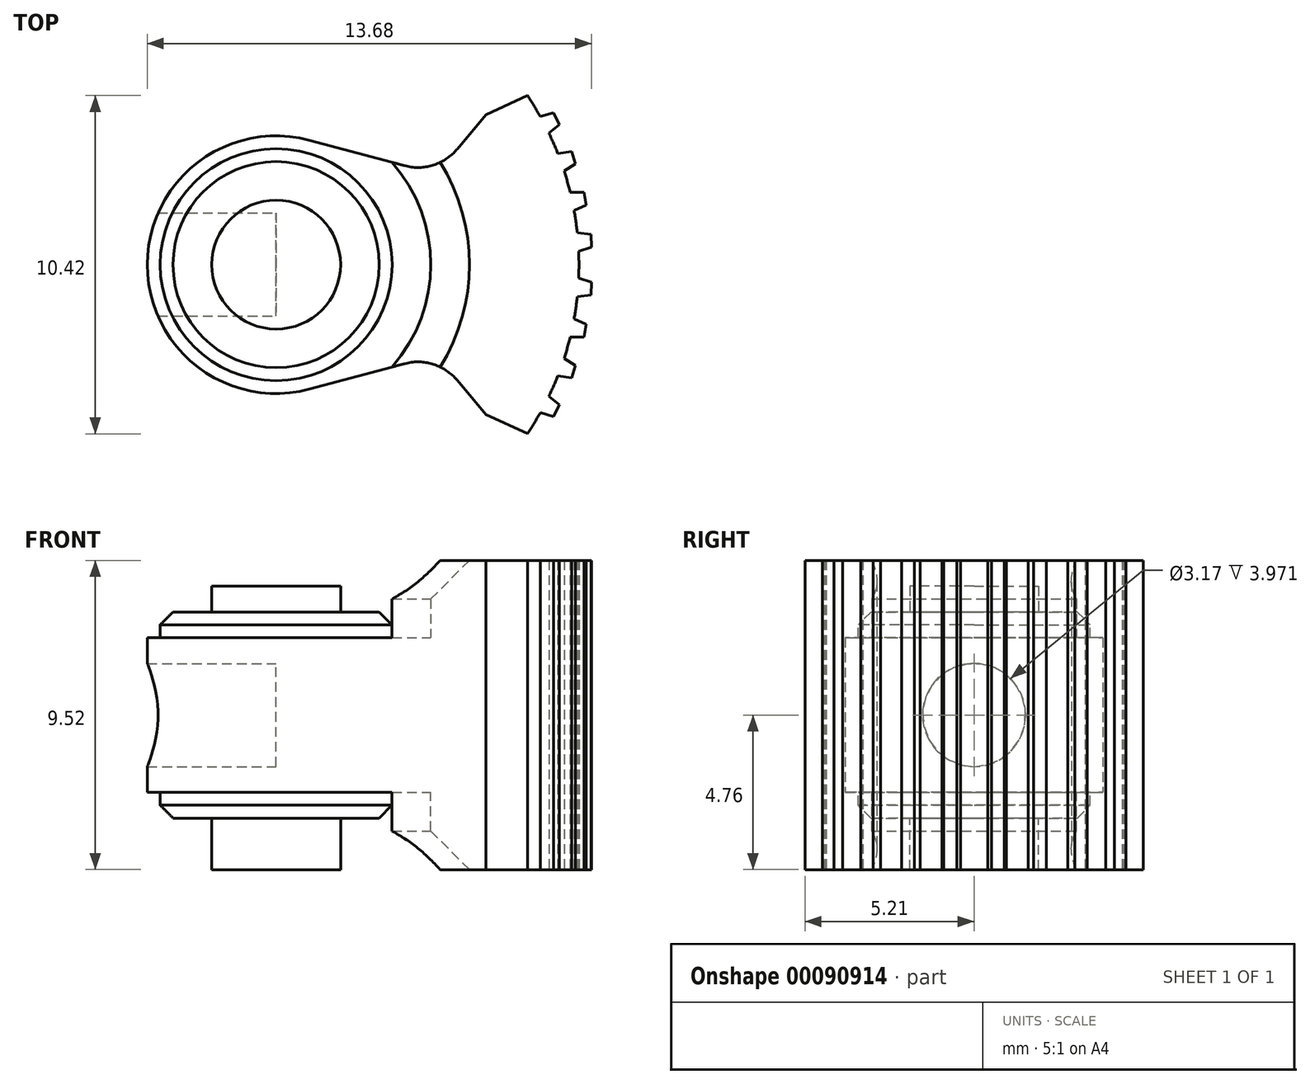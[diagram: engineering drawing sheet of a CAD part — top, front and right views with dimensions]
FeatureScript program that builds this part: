
annotation { "Feature Type Name" : "Feature", "Feature Type Description" : "" }
export const myFeature = defineFeature(function(context is Context, id is Id, definition is map)
    precondition{}
    {
        {
            var Q0;
            Q0=qCreatedBy(makeId("Top.planeOp"),FACE);
            var sketch = newSketch(context, id + "F0", { "sketchPlane" : qUnion([Q0])});
            skCircle(sketch, "E0", {"center": v(0, 0) * mm, "radius": 3.57 * mm});
            skCircle(sketch, "E1", {"center": v(0, 0) * mm, "radius": 1.98 * mm});
            skArc(sketch, "E2", {"start": v(3.57, -3.15) * mm, "mid": v(4.76, 0) * mm, "end": v(3.57, 3.15) * mm});
            skArc(sketch, "E3", {"start": v(6.46, -4.61) * mm, "mid": v(7.94, 0) * mm, "end": v(6.46, 4.61) * mm});
            skArc(sketch, "E4", {"start": v(7.74, -5.2) * mm, "mid": v(9.33, 0) * mm, "end": v(7.74, 5.2) * mm});
            skCircle(sketch, "E5.converted", {"center": v(0, 0) * mm, "radius": 3.97 * mm});
            skLineSegment(sketch, "E6", {"start": v(0, 0) * mm, "end": v(19.98, 0) * mm, "construction": true});
            skLineSegment(sketch, "E7", {"start": v(1.03, 3.83) * mm, "end": v(3.95, 3.05) * mm});
            skLineSegment(sketch, "E8", {"start": v(1.03, -3.83) * mm, "end": v(3.95, -3.05) * mm});
            skLineSegment(sketch, "E9", {"start": v(5.58, 3.56) * mm, "end": v(6.46, 4.61) * mm});
            skLineSegment(sketch, "E10", {"start": v(5.58, -3.56) * mm, "end": v(6.46, -4.61) * mm});
            skArc(sketch, "E11.filletArc", {"start": v(3.95, 3.05) * mm, "mid": v(4.84, 3.07) * mm, "end": v(5.58, 3.56) * mm});
            skArc(sketch, "E12.filletArc", {"start": v(5.58, -3.56) * mm, "mid": v(4.84, -3.07) * mm, "end": v(3.95, -3.05) * mm});
            skLineSegment(sketch, "E13", {"start": v(6.46, 4.61) * mm, "end": v(7.74, 5.2) * mm});
            skLineSegment(sketch, "E14", {"start": v(6.46, -4.61) * mm, "end": v(7.74, -5.2) * mm});
            skLineSegment(sketch, "E15.1.0", {"start": v(9.27, -0.99) * mm, "end": v(9.7, -0.93) * mm});
            skLineSegment(sketch, "E15.1.1", {"start": v(9.7, -0.93) * mm, "end": v(9.71, -0.53) * mm});
            skLineSegment(sketch, "E15.1.2", {"start": v(9.71, -0.53) * mm, "end": v(9.31, -0.42) * mm});
            skLineSegment(sketch, "E15.2.0", {"start": v(9.05, -2.23) * mm, "end": v(9.49, -2.23) * mm});
            skLineSegment(sketch, "E15.2.1", {"start": v(9.49, -2.23) * mm, "end": v(9.55, -1.84) * mm});
            skLineSegment(sketch, "E15.2.2", {"start": v(9.55, -1.84) * mm, "end": v(9.17, -1.67) * mm});
            skLineSegment(sketch, "E15.3.0", {"start": v(8.67, -3.42) * mm, "end": v(9.1, -3.49) * mm});
            skLineSegment(sketch, "E15.3.1", {"start": v(9.1, -3.49) * mm, "end": v(9.22, -3.1) * mm});
            skLineSegment(sketch, "E15.3.2", {"start": v(9.22, -3.1) * mm, "end": v(8.87, -2.88) * mm});
            skLineSegment(sketch, "E15.4.0", {"start": v(8.13, -4.56) * mm, "end": v(8.55, -4.68) * mm});
            skLineSegment(sketch, "E15.4.1", {"start": v(8.55, -4.68) * mm, "end": v(8.72, -4.31) * mm});
            skLineSegment(sketch, "E15.4.2", {"start": v(8.72, -4.31) * mm, "end": v(8.4, -4.05) * mm});
            skLineSegment(sketch, "E15.anchor1", {"start": v(0, 0) * mm, "end": v(9.29, 0.84) * mm, "construction": true});
            skLineSegment(sketch, "E15.anchor2", {"start": v(0, 0) * mm, "end": v(8.4, -4.05) * mm, "construction": true});
            skLineSegment(sketch, "E16.MirrorCS", {"start": v(9.7, 0.93) * mm, "end": v(9.71, 0.53) * mm});
            skLineSegment(sketch, "E17.MirrorCS", {"start": v(9.71, 0.53) * mm, "end": v(9.31, 0.42) * mm});
            skLineSegment(sketch, "E18.MirrorCS", {"start": v(9.27, 0.99) * mm, "end": v(9.7, 0.93) * mm});
            skLineSegment(sketch, "E19.MirrorCS", {"start": v(9.05, 2.23) * mm, "end": v(9.49, 2.23) * mm});
            skLineSegment(sketch, "E20.MirrorCS", {"start": v(9.55, 1.84) * mm, "end": v(9.17, 1.67) * mm});
            skLineSegment(sketch, "E21.MirrorCS", {"start": v(9.49, 2.23) * mm, "end": v(9.55, 1.84) * mm});
            skLineSegment(sketch, "E22.MirrorCS", {"start": v(9.1, 3.49) * mm, "end": v(9.22, 3.1) * mm});
            skLineSegment(sketch, "E23.MirrorCS", {"start": v(8.67, 3.42) * mm, "end": v(9.1, 3.49) * mm});
            skLineSegment(sketch, "E24.MirrorCS", {"start": v(9.22, 3.1) * mm, "end": v(8.87, 2.88) * mm});
            skLineSegment(sketch, "E25.MirrorCS", {"start": v(8.13, 4.56) * mm, "end": v(8.55, 4.68) * mm});
            skLineSegment(sketch, "E26.MirrorCS", {"start": v(8.55, 4.68) * mm, "end": v(8.72, 4.31) * mm});
            skLineSegment(sketch, "E27.MirrorCS", {"start": v(8.72, 4.31) * mm, "end": v(8.4, 4.05) * mm});
            skSolve(sketch);
        }
        {
            var Q0;
            Q0=makeQuery(id+"F0.imprint","IMPRINT",FACE,{"disambiguationData":[TD([[makeQuery(id+"F0.imprint","IMPRINT",EDGE,{"derivedFrom":sQuery(id+"F0.wireOp",EDGE,"E1")}),1.0]])]});
            var Q1;
            Q1=makeQuery(id+"F0.imprint","IMPRINT",FACE,{"disambiguationData":[TD([[makeQuery(id+"F0.imprint","IMPRINT",EDGE,{"derivedFrom":sQuery(id+"F0.wireOp",EDGE,"E0")}),1.0]])]});
            var Q2;
            Q2=makeQuery(id+"F0.imprint","IMPRINT",FACE,{"disambiguationData":[TD([[makeQuery(id+"F0.imprint","IMPRINT",EDGE,{"derivedFrom":sQuery(id+"F0.wireOp",EDGE,"E0")}),-1.0]])]});
            var Q3;
            {var subQ0=sQuery(id+"F0.wireOp",EDGE,"E2");Q3=makeQuery(id+"F0.imprint","IMPRINT",FACE,{"disambiguationData":[TD([[makeQuery(id+"F0.imprint","IMPRINT",EDGE,{"derivedFrom":subQ0}),1.0]])]});}
            var Q4;
            {var subQ1=sQuery(id+"F0.wireOp",EDGE,"E2");Q4=makeQuery(id+"F0.imprint","IMPRINT",FACE,{"disambiguationData":[TD([[makeQuery(id+"F0.imprint","IMPRINT",EDGE,{"derivedFrom":subQ1}),-1.0]])]});}
            var Q5;
            Q5=makeQuery(id+"F0.imprint","IMPRINT",FACE,{"disambiguationData":[TD([[makeQuery(id+"F0.imprint","IMPRINT",EDGE,{"derivedFrom":sQuery(id+"F0.wireOp",EDGE,"E3")}),-1.0]])]});
            var Q6;
            {var subQ0=sQuery(id+"F0.wireOp",EDGE,"E15.4.0");Q6=makeQuery(id+"F0.imprint","IMPRINT",FACE,{"disambiguationData":[TD([[makeQuery(id+"F0.imprint","IMPRINT",EDGE,{"derivedFrom":subQ0}),1.0]])]});}
            var Q7;
            {var subQ0=sQuery(id+"F0.wireOp",EDGE,"E15.3.0");Q7=makeQuery(id+"F0.imprint","IMPRINT",FACE,{"disambiguationData":[TD([[makeQuery(id+"F0.imprint","IMPRINT",EDGE,{"derivedFrom":subQ0}),1.0]])]});}
            var Q8;
            {var subQ0=sQuery(id+"F0.wireOp",EDGE,"E15.2.0");Q8=makeQuery(id+"F0.imprint","IMPRINT",FACE,{"disambiguationData":[TD([[makeQuery(id+"F0.imprint","IMPRINT",EDGE,{"derivedFrom":subQ0}),1.0]])]});}
            var Q9;
            {var subQ0=sQuery(id+"F0.wireOp",EDGE,"E15.1.0");Q9=makeQuery(id+"F0.imprint","IMPRINT",FACE,{"disambiguationData":[TD([[makeQuery(id+"F0.imprint","IMPRINT",EDGE,{"derivedFrom":subQ0}),1.0]])]});}
            var Q10;
            Q10=makeQuery(id+"F0.imprint","IMPRINT",FACE,{"disambiguationData":[TD([[makeQuery(id+"F0.imprint","IMPRINT",EDGE,{"derivedFrom":sQuery(id+"F0.wireOp",EDGE,"E16.MirrorCS")}),-1.0]])]});
            var Q11;
            {var subQ0=sQuery(id+"F0.wireOp",EDGE,"E19.MirrorCS");Q11=makeQuery(id+"F0.imprint","IMPRINT",FACE,{"disambiguationData":[TD([[makeQuery(id+"F0.imprint","IMPRINT",EDGE,{"derivedFrom":subQ0}),-1.0]])]});}
            var Q12;
            Q12=makeQuery(id+"F0.imprint","IMPRINT",FACE,{"disambiguationData":[TD([[makeQuery(id+"F0.imprint","IMPRINT",EDGE,{"derivedFrom":sQuery(id+"F0.wireOp",EDGE,"E22.MirrorCS")}),-1.0]])]});
            var Q13;
            {var subQ0=sQuery(id+"F0.wireOp",EDGE,"E25.MirrorCS");Q13=makeQuery(id+"F0.imprint","IMPRINT",FACE,{"disambiguationData":[TD([[makeQuery(id+"F0.imprint","IMPRINT",EDGE,{"derivedFrom":subQ0}),-1.0]])]});}
            extrude(context, id + "F1", {"entities" : qUnion([Q0, Q1, Q2, Q3, Q4, Q5, Q6, Q7, Q8, Q9, Q10, Q11, Q12, Q13]), "endBound" : BoundingType.SYMMETRIC, "depth" : 9.52 * mm});
        }
        {
            var Q0;
            Q0=makeQuery(id+"F1.opExtrude","CAP_FACE",FACE,{"disambiguationData":[OSD([sQuery(id+"F0.wireOp",EDGE,"E4"),sQuery(id+"F0.wireOp",EDGE,"E5.converted"),sQuery(id+"F0.wireOp",EDGE,"E7"),sQuery(id+"F0.wireOp",EDGE,"E8"),sQuery(id+"F0.wireOp",EDGE,"E9"),sQuery(id+"F0.wireOp",EDGE,"E10"),sQuery(id+"F0.wireOp",EDGE,"E11.filletArc"),sQuery(id+"F0.wireOp",EDGE,"E12.filletArc"),sQuery(id+"F0.wireOp",EDGE,"E13"),sQuery(id+"F0.wireOp",EDGE,"E14"),sQuery(id+"F0.wireOp",EDGE,"E15.1.0"),sQuery(id+"F0.wireOp",EDGE,"E15.1.1"),sQuery(id+"F0.wireOp",EDGE,"E15.1.2"),sQuery(id+"F0.wireOp",EDGE,"E15.2.0"),sQuery(id+"F0.wireOp",EDGE,"E15.2.1"),sQuery(id+"F0.wireOp",EDGE,"E15.2.2"),sQuery(id+"F0.wireOp",EDGE,"E15.3.0"),sQuery(id+"F0.wireOp",EDGE,"E15.3.1"),sQuery(id+"F0.wireOp",EDGE,"E15.3.2"),sQuery(id+"F0.wireOp",EDGE,"E15.4.0"),sQuery(id+"F0.wireOp",EDGE,"E15.4.1"),sQuery(id+"F0.wireOp",EDGE,"E15.4.2"),sQuery(id+"F0.wireOp",EDGE,"E16.MirrorCS"),sQuery(id+"F0.wireOp",EDGE,"E17.MirrorCS"),sQuery(id+"F0.wireOp",EDGE,"E18.MirrorCS"),sQuery(id+"F0.wireOp",EDGE,"E19.MirrorCS"),sQuery(id+"F0.wireOp",EDGE,"E20.MirrorCS"),sQuery(id+"F0.wireOp",EDGE,"E21.MirrorCS"),sQuery(id+"F0.wireOp",EDGE,"E22.MirrorCS"),sQuery(id+"F0.wireOp",EDGE,"E23.MirrorCS"),sQuery(id+"F0.wireOp",EDGE,"E24.MirrorCS"),sQuery(id+"F0.wireOp",EDGE,"E25.MirrorCS"),sQuery(id+"F0.wireOp",EDGE,"E26.MirrorCS"),sQuery(id+"F0.wireOp",EDGE,"E27.MirrorCS")])],"isStart":false});
            var Q1;
            Q1 = qBodyType(qCreatedBy(id + "F3" ,EDGE), BodyType.WIRE);
            cPlane(context, id + "F2", {"entities" : qUnion([Q0, Q1]), "cplaneType" : CPlaneType.OFFSET, "offset" : 2.38 * mm, "oppositeDirection" : true, "width" : 152.4 * mm, "height" : 152.4 * mm});
        }
        {
            var Q0;
            Q0=qCreatedBy(id+"F2.planeOp",FACE);
            var sketch = newSketch(context, id + "F3", { "sketchPlane" : qUnion([Q0])});
            skCircle(sketch, "E28", {"center": v(0, 0) * mm, "radius": 4.76 * mm});
            skSolve(sketch);
        }
        {
            var Q0;
            Q0=makeQuery(id+"F3.imprint","IMPRINT",FACE,{"disambiguationData":[TD([[makeQuery(id+"F3.imprint","IMPRINT",EDGE,{"derivedFrom":sQuery(id+"F3.wireOp",EDGE,"E28")}),1.0]])]});
            extrude(context, id + "F4", {"entities" : qUnion([Q0]), "operationType" : NewBodyOperationType.REMOVE, "depth" : 6.35 * mm});
        }
        {
            var Q0;
            Q0=makeQuery(id+"F1.opExtrude","CAP_FACE",FACE,{"disambiguationData":[OSD([sQuery(id+"F0.wireOp",EDGE,"E4"),sQuery(id+"F0.wireOp",EDGE,"E5.converted"),sQuery(id+"F0.wireOp",EDGE,"E7"),sQuery(id+"F0.wireOp",EDGE,"E8"),sQuery(id+"F0.wireOp",EDGE,"E9"),sQuery(id+"F0.wireOp",EDGE,"E10"),sQuery(id+"F0.wireOp",EDGE,"E11.filletArc"),sQuery(id+"F0.wireOp",EDGE,"E12.filletArc"),sQuery(id+"F0.wireOp",EDGE,"E13"),sQuery(id+"F0.wireOp",EDGE,"E14"),sQuery(id+"F0.wireOp",EDGE,"E15.1.0"),sQuery(id+"F0.wireOp",EDGE,"E15.1.1"),sQuery(id+"F0.wireOp",EDGE,"E15.1.2"),sQuery(id+"F0.wireOp",EDGE,"E15.2.0"),sQuery(id+"F0.wireOp",EDGE,"E15.2.1"),sQuery(id+"F0.wireOp",EDGE,"E15.2.2"),sQuery(id+"F0.wireOp",EDGE,"E15.3.0"),sQuery(id+"F0.wireOp",EDGE,"E15.3.1"),sQuery(id+"F0.wireOp",EDGE,"E15.3.2"),sQuery(id+"F0.wireOp",EDGE,"E15.4.0"),sQuery(id+"F0.wireOp",EDGE,"E15.4.1"),sQuery(id+"F0.wireOp",EDGE,"E15.4.2"),sQuery(id+"F0.wireOp",EDGE,"E16.MirrorCS"),sQuery(id+"F0.wireOp",EDGE,"E17.MirrorCS"),sQuery(id+"F0.wireOp",EDGE,"E18.MirrorCS"),sQuery(id+"F0.wireOp",EDGE,"E19.MirrorCS"),sQuery(id+"F0.wireOp",EDGE,"E20.MirrorCS"),sQuery(id+"F0.wireOp",EDGE,"E21.MirrorCS"),sQuery(id+"F0.wireOp",EDGE,"E22.MirrorCS"),sQuery(id+"F0.wireOp",EDGE,"E23.MirrorCS"),sQuery(id+"F0.wireOp",EDGE,"E24.MirrorCS"),sQuery(id+"F0.wireOp",EDGE,"E25.MirrorCS"),sQuery(id+"F0.wireOp",EDGE,"E26.MirrorCS"),sQuery(id+"F0.wireOp",EDGE,"E27.MirrorCS")])],"isStart":true});
            cPlane(context, id + "F5", {"entities" : qUnion([Q0]), "cplaneType" : CPlaneType.OFFSET, "offset" : 4.76 * mm, "oppositeDirection" : true, "width" : 152.4 * mm, "height" : 152.4 * mm});
        }
        {
            var Q0;
            Q0=makeQuery(id+"F1.opExtrude","CAP_FACE",FACE,{"disambiguationData":[OSD([sQuery(id+"F0.wireOp",EDGE,"E4"),sQuery(id+"F0.wireOp",EDGE,"E5.converted"),sQuery(id+"F0.wireOp",EDGE,"E7"),sQuery(id+"F0.wireOp",EDGE,"E8"),sQuery(id+"F0.wireOp",EDGE,"E9"),sQuery(id+"F0.wireOp",EDGE,"E10"),sQuery(id+"F0.wireOp",EDGE,"E11.filletArc"),sQuery(id+"F0.wireOp",EDGE,"E12.filletArc"),sQuery(id+"F0.wireOp",EDGE,"E13"),sQuery(id+"F0.wireOp",EDGE,"E14"),sQuery(id+"F0.wireOp",EDGE,"E15.1.0"),sQuery(id+"F0.wireOp",EDGE,"E15.1.1"),sQuery(id+"F0.wireOp",EDGE,"E15.1.2"),sQuery(id+"F0.wireOp",EDGE,"E15.2.0"),sQuery(id+"F0.wireOp",EDGE,"E15.2.1"),sQuery(id+"F0.wireOp",EDGE,"E15.2.2"),sQuery(id+"F0.wireOp",EDGE,"E15.3.0"),sQuery(id+"F0.wireOp",EDGE,"E15.3.1"),sQuery(id+"F0.wireOp",EDGE,"E15.3.2"),sQuery(id+"F0.wireOp",EDGE,"E15.4.0"),sQuery(id+"F0.wireOp",EDGE,"E15.4.1"),sQuery(id+"F0.wireOp",EDGE,"E15.4.2"),sQuery(id+"F0.wireOp",EDGE,"E16.MirrorCS"),sQuery(id+"F0.wireOp",EDGE,"E17.MirrorCS"),sQuery(id+"F0.wireOp",EDGE,"E18.MirrorCS"),sQuery(id+"F0.wireOp",EDGE,"E19.MirrorCS"),sQuery(id+"F0.wireOp",EDGE,"E20.MirrorCS"),sQuery(id+"F0.wireOp",EDGE,"E21.MirrorCS"),sQuery(id+"F0.wireOp",EDGE,"E22.MirrorCS"),sQuery(id+"F0.wireOp",EDGE,"E23.MirrorCS"),sQuery(id+"F0.wireOp",EDGE,"E24.MirrorCS"),sQuery(id+"F0.wireOp",EDGE,"E25.MirrorCS"),sQuery(id+"F0.wireOp",EDGE,"E26.MirrorCS"),sQuery(id+"F0.wireOp",EDGE,"E27.MirrorCS")])],"isStart":true});
            cPlane(context, id + "F6", {"entities" : qUnion([Q0]), "cplaneType" : CPlaneType.OFFSET, "offset" : 2.38 * mm, "oppositeDirection" : true, "width" : 152.4 * mm, "height" : 152.4 * mm});
        }
        {
            var Q0;
            Q0=qCreatedBy(id+"F6.planeOp",FACE);
            var sketch = newSketch(context, id + "F7", { "sketchPlane" : qUnion([Q0])});
            skCircle(sketch, "E29", {"center": v(0, 0) * mm, "radius": 4.76 * mm});
            skSolve(sketch);
        }
        {
            var Q0;
            Q0=makeQuery(id+"F7.imprint","IMPRINT",FACE,{"disambiguationData":[TD([[makeQuery(id+"F7.imprint","IMPRINT",EDGE,{"derivedFrom":sQuery(id+"F7.wireOp",EDGE,"E29")}),1.0]])]});
            extrude(context, id + "F8", {"entities" : qUnion([Q0]), "operationType" : NewBodyOperationType.REMOVE, "depth" : 4.3 * mm});
        }
        {
            var Q0;
            Q0=qCreatedBy(id+"F5.planeOp",FACE);
            var sketch = newSketch(context, id + "F9", { "sketchPlane" : qUnion([Q0])});
            skCircle(sketch, "E30", {"center": v(0, 0) * mm, "radius": 3.57 * mm});
            skSolve(sketch);
        }
        {
            var Q0;
            Q0 = qSketchRegion(id + "F9", true);
            extrude(context, id + "F10", {"entities" : qUnion([Q0]), "operationType" : NewBodyOperationType.ADD, "endBound" : BoundingType.SYMMETRIC, "depth" : 6.35 * mm});
        }
        {
            var Q0;
            Q0=qCreatedBy(id+"F2.planeOp",FACE);
            var sketch = newSketch(context, id + "F11", { "sketchPlane" : qUnion([Q0])});
            skCircle(sketch, "E31", {"center": v(0, 0) * mm, "radius": 1.98 * mm});
            skSolve(sketch);
        }
        {
            var Q0;
            Q0 = qSketchRegion(id + "F11", true);
            extrude(context, id + "F12", {"entities" : qUnion([Q0]), "operationType" : NewBodyOperationType.ADD, "depth" : 1.59 * mm});
        }
        {
            var Q0;
            Q0=qCreatedBy(id+"F6.planeOp",FACE);
            var sketch = newSketch(context, id + "F13", { "sketchPlane" : qUnion([Q0])});
            skCircle(sketch, "E32", {"center": v(0, 0) * mm, "radius": 1.98 * mm});
            skSolve(sketch);
        }
        {
            var Q0;
            Q0 = qSketchRegion(id + "F13", true);
            extrude(context, id + "F14", {"entities" : qUnion([Q0]), "operationType" : NewBodyOperationType.ADD, "depth" : 2.38 * mm});
        }
        {
            var Q0;
            Q0=qCreatedBy(makeId("Right.planeOp"),FACE);
            var sketch = newSketch(context, id + "F15", { "sketchPlane" : qUnion([Q0])});
            skCircle(sketch, "E33", {"center": v(0, 0) * mm, "radius": 1.59 * mm});
            skSolve(sketch);
        }
        {
            var Q0;
            Q0 = qSketchRegion(id + "F15", true);
            extrude(context, id + "F16", {"entities" : qUnion([Q0]), "operationType" : NewBodyOperationType.REMOVE, "oppositeDirection" : true, "depth" : 8.64 * mm});
        }
        {
            var Q0;
            Q0=makeQuery(id+"F4.boolean.opBoolean","INTERSECT",EDGE,{"derivedFrom":[makeQuery(id+"F1.opExtrude","CAP_FACE",FACE,{"disambiguationData":[OSD([sQuery(id+"F0.wireOp",EDGE,"E4"),sQuery(id+"F0.wireOp",EDGE,"E5.converted"),sQuery(id+"F0.wireOp",EDGE,"E7"),sQuery(id+"F0.wireOp",EDGE,"E8"),sQuery(id+"F0.wireOp",EDGE,"E9"),sQuery(id+"F0.wireOp",EDGE,"E10"),sQuery(id+"F0.wireOp",EDGE,"E11.filletArc"),sQuery(id+"F0.wireOp",EDGE,"E12.filletArc"),sQuery(id+"F0.wireOp",EDGE,"E13"),sQuery(id+"F0.wireOp",EDGE,"E14"),sQuery(id+"F0.wireOp",EDGE,"E15.1.0"),sQuery(id+"F0.wireOp",EDGE,"E15.1.1"),sQuery(id+"F0.wireOp",EDGE,"E15.1.2"),sQuery(id+"F0.wireOp",EDGE,"E15.2.0"),sQuery(id+"F0.wireOp",EDGE,"E15.2.1"),sQuery(id+"F0.wireOp",EDGE,"E15.2.2"),sQuery(id+"F0.wireOp",EDGE,"E15.3.0"),sQuery(id+"F0.wireOp",EDGE,"E15.3.1"),sQuery(id+"F0.wireOp",EDGE,"E15.3.2"),sQuery(id+"F0.wireOp",EDGE,"E15.4.0"),sQuery(id+"F0.wireOp",EDGE,"E15.4.1"),sQuery(id+"F0.wireOp",EDGE,"E15.4.2"),sQuery(id+"F0.wireOp",EDGE,"E16.MirrorCS"),sQuery(id+"F0.wireOp",EDGE,"E17.MirrorCS"),sQuery(id+"F0.wireOp",EDGE,"E18.MirrorCS"),sQuery(id+"F0.wireOp",EDGE,"E19.MirrorCS"),sQuery(id+"F0.wireOp",EDGE,"E20.MirrorCS"),sQuery(id+"F0.wireOp",EDGE,"E21.MirrorCS"),sQuery(id+"F0.wireOp",EDGE,"E22.MirrorCS"),sQuery(id+"F0.wireOp",EDGE,"E23.MirrorCS"),sQuery(id+"F0.wireOp",EDGE,"E24.MirrorCS"),sQuery(id+"F0.wireOp",EDGE,"E25.MirrorCS"),sQuery(id+"F0.wireOp",EDGE,"E26.MirrorCS"),sQuery(id+"F0.wireOp",EDGE,"E27.MirrorCS")])],"isStart":false}),makeQuery(id+"F4.opExtrude","SWEPT_FACE",FACE,{"disambiguationData":[OSD([sQuery(id+"F3.wireOp",EDGE,"E28")])]})]});
            chamfer(context, id + "F17", {"entities" : qUnion([Q0]), "chamferType" : ChamferType.OFFSET_ANGLE, "width" : 1.2 * mm, "oppositeDirection" : false, "angle" : 45 * degree, "tangentPropagation" : true});
        }
        {
            var Q0;
            Q0=makeQuery(id+"F8.boolean.opBoolean","INTERSECT",EDGE,{"derivedFrom":[makeQuery(id+"F1.opExtrude","CAP_FACE",FACE,{"disambiguationData":[OSD([sQuery(id+"F0.wireOp",EDGE,"E4"),sQuery(id+"F0.wireOp",EDGE,"E5.converted"),sQuery(id+"F0.wireOp",EDGE,"E7"),sQuery(id+"F0.wireOp",EDGE,"E8"),sQuery(id+"F0.wireOp",EDGE,"E9"),sQuery(id+"F0.wireOp",EDGE,"E10"),sQuery(id+"F0.wireOp",EDGE,"E11.filletArc"),sQuery(id+"F0.wireOp",EDGE,"E12.filletArc"),sQuery(id+"F0.wireOp",EDGE,"E13"),sQuery(id+"F0.wireOp",EDGE,"E14"),sQuery(id+"F0.wireOp",EDGE,"E15.1.0"),sQuery(id+"F0.wireOp",EDGE,"E15.1.1"),sQuery(id+"F0.wireOp",EDGE,"E15.1.2"),sQuery(id+"F0.wireOp",EDGE,"E15.2.0"),sQuery(id+"F0.wireOp",EDGE,"E15.2.1"),sQuery(id+"F0.wireOp",EDGE,"E15.2.2"),sQuery(id+"F0.wireOp",EDGE,"E15.3.0"),sQuery(id+"F0.wireOp",EDGE,"E15.3.1"),sQuery(id+"F0.wireOp",EDGE,"E15.3.2"),sQuery(id+"F0.wireOp",EDGE,"E15.4.0"),sQuery(id+"F0.wireOp",EDGE,"E15.4.1"),sQuery(id+"F0.wireOp",EDGE,"E15.4.2"),sQuery(id+"F0.wireOp",EDGE,"E16.MirrorCS"),sQuery(id+"F0.wireOp",EDGE,"E17.MirrorCS"),sQuery(id+"F0.wireOp",EDGE,"E18.MirrorCS"),sQuery(id+"F0.wireOp",EDGE,"E19.MirrorCS"),sQuery(id+"F0.wireOp",EDGE,"E20.MirrorCS"),sQuery(id+"F0.wireOp",EDGE,"E21.MirrorCS"),sQuery(id+"F0.wireOp",EDGE,"E22.MirrorCS"),sQuery(id+"F0.wireOp",EDGE,"E23.MirrorCS"),sQuery(id+"F0.wireOp",EDGE,"E24.MirrorCS"),sQuery(id+"F0.wireOp",EDGE,"E25.MirrorCS"),sQuery(id+"F0.wireOp",EDGE,"E26.MirrorCS"),sQuery(id+"F0.wireOp",EDGE,"E27.MirrorCS")])],"isStart":true}),makeQuery(id+"F8.opExtrude","SWEPT_FACE",FACE,{"disambiguationData":[OSD([sQuery(id+"F7.wireOp",EDGE,"E29")])]})]});
            chamfer(context, id + "F18", {"entities" : qUnion([Q0]), "chamferType" : ChamferType.OFFSET_ANGLE, "width" : 1.2 * mm, "oppositeDirection" : false, "angle" : 45 * degree, "tangentPropagation" : true});
        }
        {
            var Q0;
            Q0=makeQuery(id+"F10.opExtrude","CAP_EDGE",EDGE,{"disambiguationData":[OSD([sQuery(id+"F9.wireOp",EDGE,"E30")])],"isStart":true});
            chamfer(context, id + "F19", {"entities" : qUnion([Q0]), "chamferType" : ChamferType.OFFSET_ANGLE, "width" : 0.4 * mm, "oppositeDirection" : false, "angle" : 45 * degree, "tangentPropagation" : true});
        }
        {
            var Q0;
            Q0=makeQuery(id+"F10.opExtrude","CAP_EDGE",EDGE,{"disambiguationData":[OSD([sQuery(id+"F9.wireOp",EDGE,"E30")])],"isStart":false});
            chamfer(context, id + "F20", {"entities" : qUnion([Q0]), "chamferType" : ChamferType.OFFSET_ANGLE, "width" : 0.4 * mm, "oppositeDirection" : false, "angle" : 45 * degree, "tangentPropagation" : true});
        }
    });
